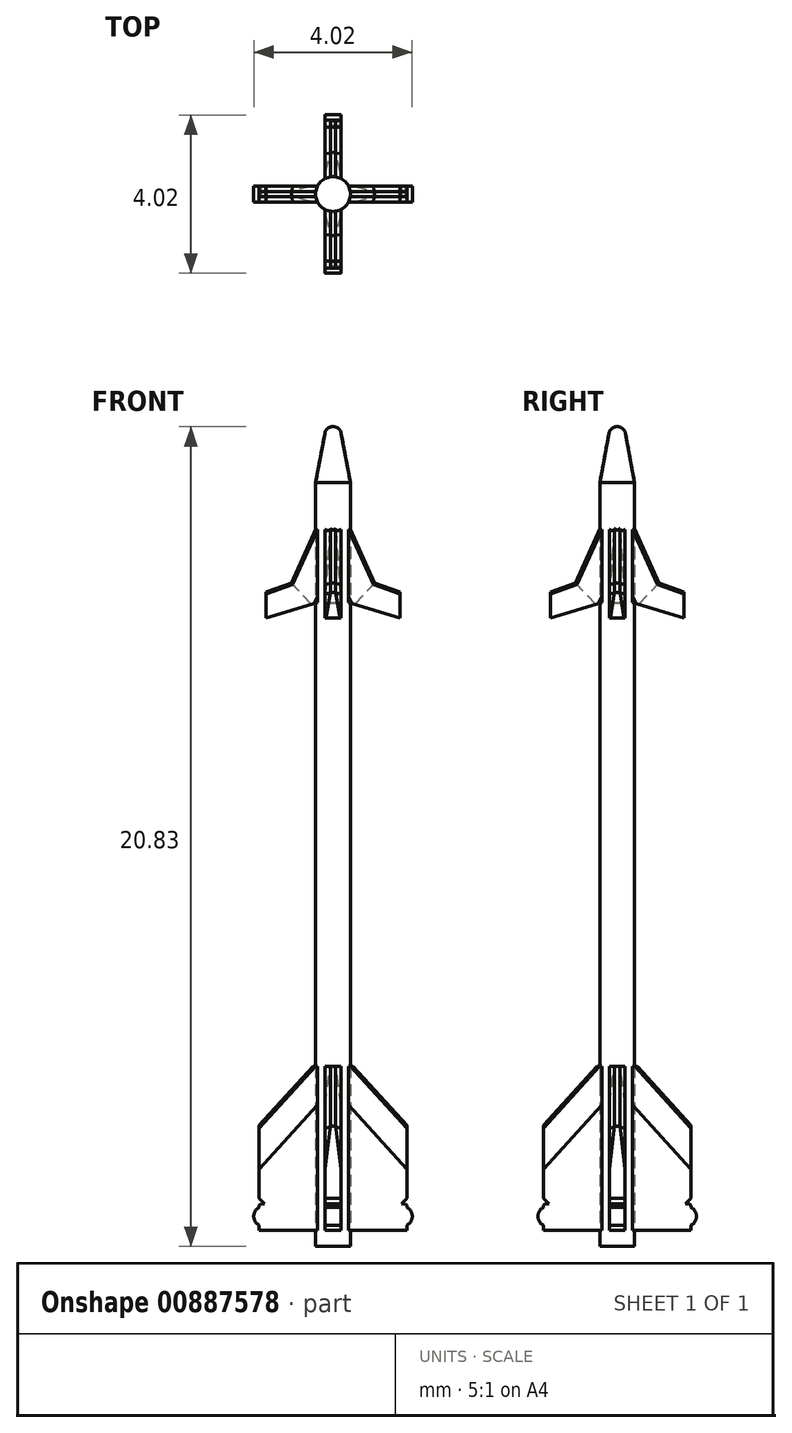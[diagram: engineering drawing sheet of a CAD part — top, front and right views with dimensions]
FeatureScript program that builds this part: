
annotation { "Feature Type Name" : "Feature", "Feature Type Description" : "" }
export const myFeature = defineFeature(function(context is Context, id is Id, definition is map)
    precondition{}
    {
        {
            var Q0;
            Q0=qCreatedBy(makeId("Front.planeOp"),FACE);
            var sketch = newSketch(context, id + "F0", { "sketchPlane" : qUnion([Q0])});
            skLineSegment(sketch, "E0", {"start": v(0, 0) * mm, "end": v(0, 20.83) * mm});
            skLineSegment(sketch, "E1", {"start": v(0.44, 19.4) * mm, "end": v(0.44, 0) * mm});
            skLineSegment(sketch, "E2", {"start": v(0.44, 0) * mm, "end": v(0, 0) * mm});
            skLineSegment(sketch, "E3", {"start": v(0, 20.83) * mm, "end": v(1.85, 20.83) * mm, "construction": true});
            skLineSegment(sketch, "E4", {"start": v(0.44, 19.4) * mm, "end": v(0.2, 20.66) * mm});
            skArc(sketch, "E5", {"start": v(0.2, 20.66) * mm, "mid": v(0.14, 20.78) * mm, "end": v(0, 20.83) * mm});
            skSolve(sketch);
        }
        {
            var Q0;
            Q0=qSketchRegion(id+"F0",true);
            var Q1;
            Q1=sQuery(id+"F0.wireOp",EDGE,"E0");
            revolve(context, id + "F1", {"surfaceOperationType" : NewSurfaceOperationType.NEW, "entities" : qUnion([Q0]), "axis" : qUnion([Q1]), "revolveType" : RevolveType.FULL});
        }
        {
            var Q0;
            Q0=qCreatedBy(makeId("Front.planeOp"),FACE);
            var sketch = newSketch(context, id + "F2", { "sketchPlane" : qUnion([Q0])});
            skLineSegment(sketch, "E6", {"start": v(0.65, 4.58) * mm, "end": v(-0.65, 4.58) * mm});
            skLineSegment(sketch, "E7", {"start": v(-1.88, 3.23) * mm, "end": v(-0.65, 4.58) * mm});
            skLineSegment(sketch, "E8", {"start": v(-1.87, 3.23) * mm, "end": v(-1.87, 1.23) * mm});
            skLineSegment(sketch, "E9", {"start": v(1.88, 1.23) * mm, "end": v(1.88, 3.23) * mm});
            skLineSegment(sketch, "E10", {"start": v(0.65, 4.58) * mm, "end": v(1.88, 3.23) * mm});
            skLineSegment(sketch, "E11", {"start": v(0, 0) * mm, "end": v(0, 4.58) * mm, "construction": true});
            skLineSegment(sketch, "E12", {"start": v(-0.44, 0.8) * mm, "end": v(-0.44, 4.16) * mm, "construction": true});
            skLineSegment(sketch, "E13.0", {"start": v(0.44, 19.4) * mm, "end": v(-0.44, 19.4) * mm});
            skLineSegment(sketch, "E14", {"start": v(-1.87, 0.42) * mm, "end": v(-1.87, 0.54) * mm});
            skLineSegment(sketch, "E15", {"start": v(1.88, 0.42) * mm, "end": v(1.88, 0.54) * mm});
            skLineSegment(sketch, "E16", {"start": v(1.88, 1.23) * mm, "end": v(1.74, 1.1) * mm});
            skLineSegment(sketch, "E17", {"start": v(1.88, 1.05) * mm, "end": v(1.88, 1) * mm});
            skLineSegment(sketch, "E18", {"start": v(-1.88, 1.23) * mm, "end": v(-1.74, 1.1) * mm});
            skLineSegment(sketch, "E19", {"start": v(-1.87, 1.05) * mm, "end": v(-1.87, 1) * mm});
            skArc(sketch, "E20", {"start": v(-1.88, 1) * mm, "mid": v(-2.01, 0.77) * mm, "end": v(-1.87, 0.54) * mm});
            skArc(sketch, "E21", {"start": v(1.88, 0.54) * mm, "mid": v(2.01, 0.77) * mm, "end": v(1.88, 1) * mm});
            skLineSegment(sketch, "E22", {"start": v(-1.88, 1.05) * mm, "end": v(-1.83, 1.1) * mm});
            skLineSegment(sketch, "E23", {"start": v(-1.83, 1.1) * mm, "end": v(-1.74, 1.1) * mm});
            skLineSegment(sketch, "E24", {"start": v(1.88, 1.05) * mm, "end": v(1.83, 1.1) * mm});
            skLineSegment(sketch, "E25", {"start": v(1.83, 1.1) * mm, "end": v(1.74, 1.1) * mm});
            skLineSegment(sketch, "E26", {"start": v(-1.87, 0.42) * mm, "end": v(1.88, 0.42) * mm});
            skLineSegment(sketch, "E27", {"start": v(0, 0) * mm, "end": v(0, 0.42) * mm, "construction": true});
            skLineSegment(sketch, "E28.0", {"start": v(0.44, 0) * mm, "end": v(-0.44, 0) * mm});
            skLineSegment(sketch, "E29", {"start": v(-1.7, 15.97) * mm, "end": v(0, 16.49) * mm});
            skLineSegment(sketch, "E30", {"start": v(0, 16.49) * mm, "end": v(1.7, 15.97) * mm});
            skLineSegment(sketch, "E31", {"start": v(-0.44, 18.26) * mm, "end": v(0.44, 18.26) * mm});
            skArc(sketch, "E32", {"start": v(-0.44, 18.26) * mm, "mid": v(-0.52, 18.24) * mm, "end": v(-0.58, 18.17) * mm});
            skArc(sketch, "E33", {"start": v(0.58, 18.17) * mm, "mid": v(0.52, 18.24) * mm, "end": v(0.44, 18.26) * mm});
            skPoint(sketch, "E34", {"position": v(-0.44, 16.35) * mm});
            skLineSegment(sketch, "E35", {"start": v(-0.58, 18.17) * mm, "end": v(-1.14, 16.94) * mm});
            skLineSegment(sketch, "E36", {"start": v(-1.14, 16.94) * mm, "end": v(-1.7, 16.74) * mm});
            skLineSegment(sketch, "E37", {"start": v(-1.7, 16.74) * mm, "end": v(-1.7, 15.97) * mm});
            skLineSegment(sketch, "E38", {"start": v(1.7, 15.97) * mm, "end": v(1.7, 16.74) * mm});
            skLineSegment(sketch, "E39", {"start": v(1.7, 16.74) * mm, "end": v(1.14, 16.94) * mm});
            skLineSegment(sketch, "E40", {"start": v(1.14, 16.94) * mm, "end": v(0.58, 18.17) * mm});
            skSolve(sketch);
        }
        {
            var Q0;
            Q0=qSketchRegion(id+"F2",true);
            extrude(context, id + "F3", {"entities" : qUnion([Q0]), "operationType" : NewBodyOperationType.ADD, "depth" : .4 * mm, "offsetDistance" : 25 * mm, "symmetric" : true});
        }
        {
            var Q0;
            Q0=makeQuery(id+"F3.opExtrude","CAP_EDGE",EDGE,{"disambiguationData":[OSD([sQuery(id+"F2.wireOp",EDGE,"E40")])],"isStart":false});
            var Q1;
            Q1=makeQuery(id+"F3.opExtrude","CAP_EDGE",EDGE,{"disambiguationData":[OSD([sQuery(id+"F2.wireOp",EDGE,"E39")])],"isStart":false});
            var Q2;
            Q2=makeQuery(id+"F3.opExtrude","CAP_EDGE",EDGE,{"disambiguationData":[OSD([sQuery(id+"F2.wireOp",EDGE,"E35")])],"isStart":false});
            var Q3;
            Q3=makeQuery(id+"F3.opExtrude","CAP_EDGE",EDGE,{"disambiguationData":[OSD([sQuery(id+"F2.wireOp",EDGE,"E36")])],"isStart":false});
            var Q4;
            Q4=makeQuery(id+"F3.opExtrude","CAP_EDGE",EDGE,{"disambiguationData":[OSD([sQuery(id+"F2.wireOp",EDGE,"E10")])],"isStart":true});
            var Q5;
            Q5=makeQuery(id+"F3.opExtrude","CAP_EDGE",EDGE,{"disambiguationData":[OSD([sQuery(id+"F2.wireOp",EDGE,"E7")])],"isStart":true});
            chamfer(context, id + "F4", {"entities" : qUnion([Q0, Q1, Q2, Q3, Q4, Q5]), "chamferType" : ChamferType.OFFSET_ANGLE, "width" : .15 * mm, "oppositeDirection" : true, "angle" : 80 * degree});
        }
        {
            var Q0;
            Q0=makeQuery(id+"F3.opExtrude","CAP_EDGE",EDGE,{"disambiguationData":[OSD([sQuery(id+"F2.wireOp",EDGE,"E10")])],"isStart":false});
            var Q1;
            Q1=makeQuery(id+"F3.opExtrude","CAP_EDGE",EDGE,{"disambiguationData":[OSD([sQuery(id+"F2.wireOp",EDGE,"E7")])],"isStart":false});
            var Q2;
            Q2=makeQuery(id+"F3.opExtrude","CAP_EDGE",EDGE,{"disambiguationData":[OSD([sQuery(id+"F2.wireOp",EDGE,"E39")])],"isStart":true});
            var Q3;
            Q3=makeQuery(id+"F3.opExtrude","CAP_EDGE",EDGE,{"disambiguationData":[OSD([sQuery(id+"F2.wireOp",EDGE,"E40")])],"isStart":true});
            var Q4;
            Q4=makeQuery(id+"F3.opExtrude","CAP_EDGE",EDGE,{"disambiguationData":[OSD([sQuery(id+"F2.wireOp",EDGE,"E35")])],"isStart":true});
            var Q5;
            Q5=makeQuery(id+"F3.opExtrude","CAP_EDGE",EDGE,{"disambiguationData":[OSD([sQuery(id+"F2.wireOp",EDGE,"E36")])],"isStart":true});
            chamfer(context, id + "F5", {"entities" : qUnion([Q0, Q1, Q2, Q3, Q4, Q5]), "chamferType" : ChamferType.OFFSET_ANGLE, "width" : .15 * mm, "oppositeDirection" : false, "angle" : 80 * degree});
        }
        {
            var Q0;
            Q0=makeQuery(id+"F1.opRevolve","SWEPT_BODY",BODY,{"disambiguationData":[OSD([sQuery(id+"F0.wireOp",EDGE,"E0"),sQuery(id+"F0.wireOp",EDGE,"E1"),sQuery(id+"F0.wireOp",EDGE,"E2"),sQuery(id+"F0.wireOp",EDGE,"m1K1lCZm-MTc8-Btmt-IA6e-LtdyprMEJuD3")])]});
            var Q1;
            Q1=makeQuery(id+"F1.opRevolve","SWEPT_FACE",FACE,{"disambiguationData":[OSD([sQuery(id+"F0.wireOp",EDGE,"E1")])]});
            circularPattern(context, id + "F6", {"entities" : qUnion([Q0]), "axis" : qUnion([Q1]), "angle" : 360 * degree, "instanceCount" : 4, "equalSpace" : true, "computeTransformsWithoutBuiltin" : true});
        }
    });
